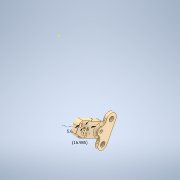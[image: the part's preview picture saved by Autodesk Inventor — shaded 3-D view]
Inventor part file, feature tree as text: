
AUTODESK INVENTOR PART (.ipt)
format: ipt  version: 2020 (Build 240168000, 168)  size: 337,408 bytes
history: native  units: in
note: dims shown in document units (in); Inventor stores cm internally (conversion verified against a paired STEP export)
features: sketch x11, extrude x7, fillet x5, projected_geometry x2
ambient origin geometry x8: Origin, YZ Plane, XZ Plane, XY Plane, X Axis, Y Axis, Z Axis, Center Point
bodies: Body1 (feature_tree)
feature tree (25):
  sketch  "Sketch3"  dims[d0=0.0039in d1=0.2362in d2=0.0in]
  sketch  "Sketch4"  dims[d3=0.315in d4=0.1575in d5=0.315in d6=0.0787in d7=0.0in d8=0.1181in]
  extrude  "Extrusion1"  Depth=0.2362in TaperAngle=0.0deg
  extrude  "Extrusion2"  Depth=0.1181in
  fillet  "Fillet1"  Radius=0.315in
  sketch  "Sketch7"  dims[d13=0.0787in d14=0.0787in d15=0.0in d16=0.2008in]
  fillet  "Fillet2"  Radius=0.0787in
  fillet  "Fillet3"  Radius=0.1181in
  extrude  "Extrusion3"  Depth=0.1181in
  extrude  "Extrusion4"  Depth=0.0787in
  sketch  "Sketch9"  dims[d22=0.3717in d23=0.0787in d27=0.1181in]
  sketch  "Sketch10"  dims[d29=0.1181in]
  sketch  "Sketch11"  dims[d30=0.315in]
  extrude  "Extrusion6"  Depth=0.0787in TaperAngle=0.0deg
  fillet  "Fillet6"  Radius=0.2008in
  extrude  "Extrusion7"  Depth=0.1181in TaperAngle=0.0deg
  extrude  "Extrusion8"  Depth=0.0787in
  fillet  "Fillet7"  Radius=0.1181in
  sketch  "Sketch5"  dims[d9=0.1102in d10=0.1181in]
  sketch  "Sketch6"  dims[d11=0.2047in d12=0.0787in]
  sketch  "Sketch8"  dims[d17=0.2008in d18=0.1181in d19=0.0in]
  projected_geometry  "Projected Loop2"
  projected_geometry  "Projected Loop3"
  sketch  "Sketch12"  dims[d31=0.3937in d32=0.0in]
  sketch  "Sketch13"  dims[d33=0.1969in d34=0.1181in d35=0.0in d36=0.2205in d37=0.1378in d38=0.0in d39=0.2205in d40=0.6687in d41=0.0787in]
